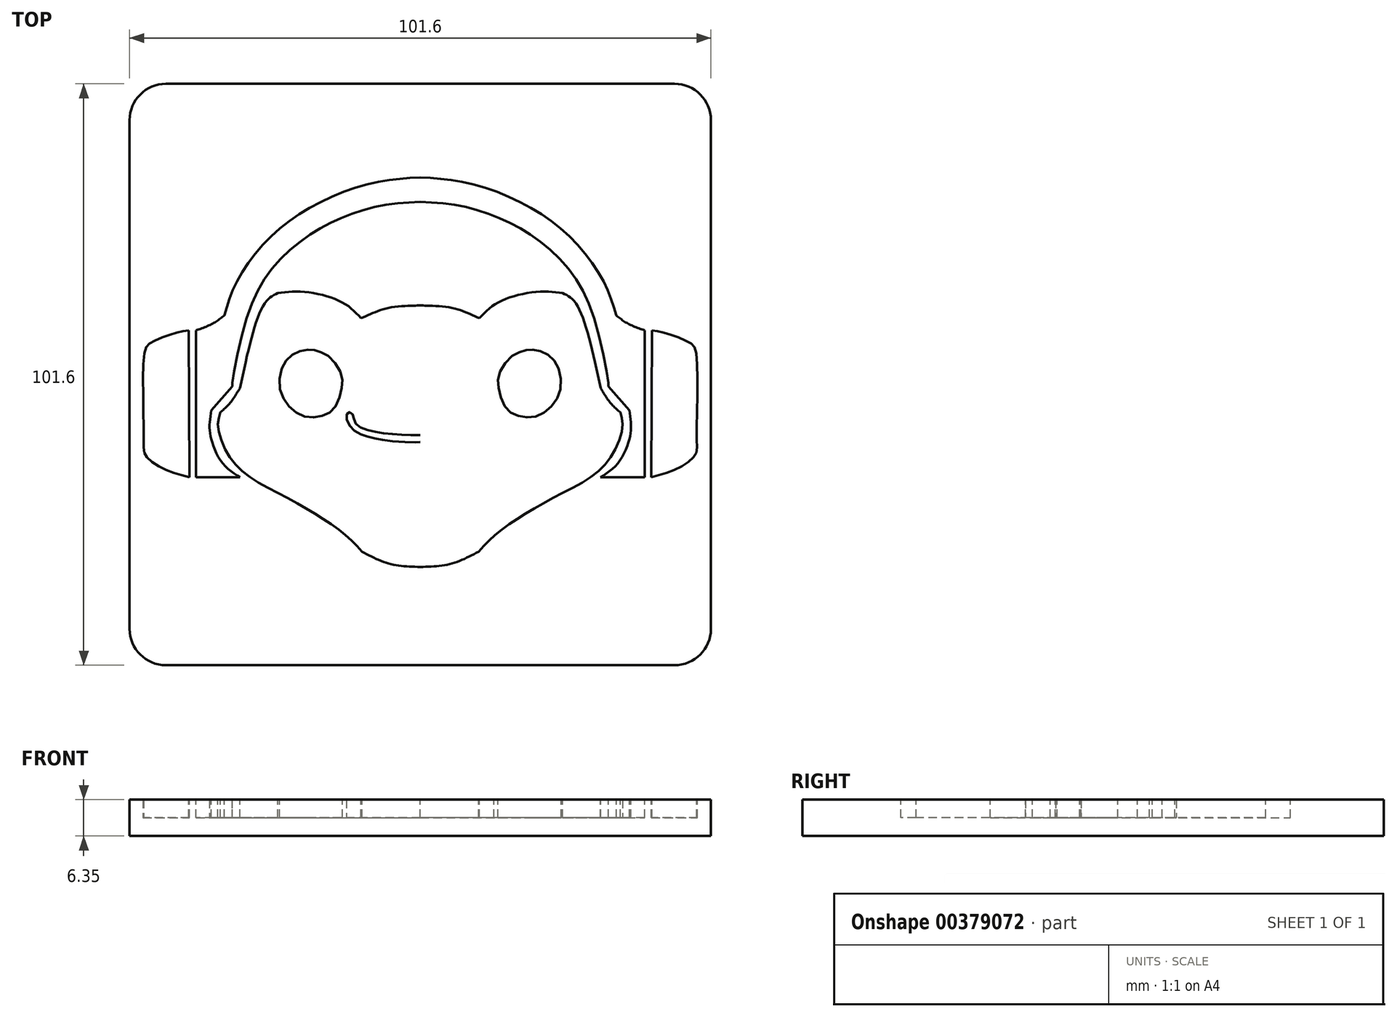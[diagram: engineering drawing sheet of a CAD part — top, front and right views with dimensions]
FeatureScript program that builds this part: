
annotation { "Feature Type Name" : "Feature", "Feature Type Description" : "" }
export const myFeature = defineFeature(function(context is Context, id is Id, definition is map)
    precondition{}
    {
        {
            var Q0;
            Q0=qCreatedBy(makeId("Top.planeOp"),FACE);
            var sketch = newSketch(context, id + "F0", { "sketchPlane" : qUnion([Q0])});
            skLineSegment(sketch, "E0.bottom", {"start": v(-44.45, 50.8) * mm, "end": v(44.45, 50.8) * mm});
            skLineSegment(sketch, "E0.top", {"start": v(-44.45, -50.8) * mm, "end": v(44.45, -50.8) * mm});
            skLineSegment(sketch, "E0.left", {"start": v(-50.8, 44.45) * mm, "end": v(-50.8, -44.45) * mm});
            skLineSegment(sketch, "E0.right", {"start": v(50.8, 44.45) * mm, "end": v(50.8, -44.45) * mm});
            skPoint(sketch, "E1.visualSharp", {"position": v(-50.8, 50.8) * mm});
            skArc(sketch, "E1.filletArc", {"start": v(-44.45, 50.8) * mm, "mid": v(-48.94, 48.94) * mm, "end": v(-50.8, 44.45) * mm});
            skPoint(sketch, "E2.visualSharp", {"position": v(50.8, 50.8) * mm});
            skArc(sketch, "E2.filletArc", {"start": v(50.8, 44.45) * mm, "mid": v(48.94, 48.94) * mm, "end": v(44.45, 50.8) * mm});
            skPoint(sketch, "E3.visualSharp", {"position": v(-50.8, -50.8) * mm});
            skArc(sketch, "E3.filletArc", {"start": v(-50.8, -44.45) * mm, "mid": v(-48.94, -48.94) * mm, "end": v(-44.45, -50.8) * mm});
            skPoint(sketch, "E4.visualSharp", {"position": v(50.8, -50.8) * mm});
            skArc(sketch, "E4.filletArc", {"start": v(44.45, -50.8) * mm, "mid": v(48.94, -48.94) * mm, "end": v(50.8, -44.45) * mm});
            skSolve(sketch);
        }
        {
            var Q0;
            Q0 = qSketchRegion(id + "F0", true);
            extrude(context, id + "F1", {"entities" : qUnion([Q0]), "depth" : 6.35 * mm});
        }
        {
            var Q0;
            Q0=makeQuery(id+"F1.opExtrude","CAP_FACE",FACE,{"disambiguationData":[OSD([sQuery(id+"F0.wireOp",EDGE,"E0.bottom"),sQuery(id+"F0.wireOp",EDGE,"E0.top"),sQuery(id+"F0.wireOp",EDGE,"E0.left"),sQuery(id+"F0.wireOp",EDGE,"E0.right"),sQuery(id+"F0.wireOp",EDGE,"E1.filletArc"),sQuery(id+"F0.wireOp",EDGE,"E2.filletArc"),sQuery(id+"F0.wireOp",EDGE,"E3.filletArc"),sQuery(id+"F0.wireOp",EDGE,"E4.filletArc")])],"isStart":false});
            var sketch = newSketch(context, id + "F2", { "sketchPlane" : qUnion([Q0])});
            skFitSpline(sketch, "E5", {"points": [v(-24.89, 14.25) * mm, v(-27.23, 12.37) * mm, v(-31.52, -2.38) * mm], "startDerivative": vector(-7.87, -3.8) * mm, "endDerivative": vector(-5.68, -26.52) * mm});
            skFitSpline(sketch, "E6", {"points": [v(-31.52, -2.38) * mm, v(-33.26, -5) * mm, v(-34.94, -6.6) * mm], "startDerivative": vector(-3.14, -5.23) * mm, "endDerivative": vector(-3.71, -3.16) * mm});
            skFitSpline(sketch, "E7", {"points": [v(-34.94, -6.6) * mm, v(-35.36, -9) * mm, v(-33.65, -13.85) * mm, v(-29.88, -17.88) * mm, v(-23.23, -21.57) * mm, v(-17.3, -25.03) * mm, v(-12.94, -28.16) * mm, v(-10.2, -30.95) * mm], "startDerivative": vector(-7.2, -21.92) * mm, "endDerivative": vector(20.36, -22.6) * mm});
            skFitSpline(sketch, "E8", {"points": [v(-10.2, -30.95) * mm, v(-5.4, -33.06) * mm, v(0, -33.63) * mm], "startDerivative": vector(9.4, -5.03) * mm, "endDerivative": vector(10.97, -0.34) * mm});
            skFitSpline(sketch, "E9", {"points": [v(-24.89, 14.25) * mm, v(-21.4, 14.5) * mm, v(-16.37, 13.7) * mm, v(-12.62, 11.97) * mm, v(-10.36, 9.83) * mm], "startDerivative": vector(13.95, 1.85) * mm, "endDerivative": vector(9.25, -10.17) * mm});
            skFitSpline(sketch, "E10", {"points": [v(-10.36, 9.83) * mm, v(-8, 10.86) * mm, v(-4.88, 11.76) * mm, v(-1.13, 12.04) * mm, v(0, 12.06) * mm], "startDerivative": vector(9.19, 4.21) * mm, "endDerivative": vector(5.68, 0.03) * mm});
            skFitSpline(sketch, "E11", {"points": [v(-19.65, 4.33) * mm, v(-22.07, 3.64) * mm, v(-23.97, 1.58) * mm, v(-24.54, -2.38) * mm, v(-22.9, -5.56) * mm, v(-20.13, -7.33) * mm, v(-17.2, -7.26) * mm, v(-14.99, -5.87) * mm, v(-13.75, -2.55) * mm, v(-13.78, 0) * mm, v(-15.84, 3.05) * mm, v(-18.04, 4.14) * mm, v(-19.65, 4.33) * mm]});
            skFitSpline(sketch, "E12", {"points": [v(0, -10.6) * mm, v(-5.07, -10.4) * mm, v(-9.16, -9.73) * mm, v(-11.3, -8.53) * mm, v(-11.74, -7.1) * mm, v(-12.43, -6.56) * mm, v(-12.9, -7.3) * mm, v(-11.85, -9.5) * mm, v(-9.16, -10.87) * mm, v(-5.1, -11.61) * mm, v(0, -11.8) * mm, v(0, -11.77) * mm], "startDerivative": vector(-38.3, 0.78) * mm, "endDerivative": vector(-1.42, 2.68) * mm});
            skFitSpline(sketch, "E13", {"points": [v(0, 30.15) * mm, v(-6.76, 29.52) * mm, v(-13.7, 27.37) * mm, v(-19.95, 23.97) * mm, v(-26.25, 18.03) * mm, v(-30.84, 8.17) * mm, v(-32.9, -2.1) * mm, v(-32.86, -2.1) * mm], "startDerivative": vector(-45.5, -2.07) * mm, "endDerivative": vector(3.29, 1.57) * mm});
            skFitSpline(sketch, "E14", {"points": [v(-32.86, -2.1) * mm, v(-36.53, -6.27) * mm], "startDerivative": vector(-3.67, -4.17) * mm, "endDerivative": vector(-3.67, -4.17) * mm});
            skFitSpline(sketch, "E15", {"points": [v(-36.53, -6.27) * mm, v(-36.82, -8.85) * mm, v(-36.53, -11.28) * mm, v(-34.68, -15.33) * mm, v(-31.5, -17.97) * mm], "startDerivative": vector(-1.76, -12.05) * mm, "endDerivative": vector(12.4, -8.07) * mm});
            skFitSpline(sketch, "E16", {"points": [v(-31.5, -17.97) * mm, v(-39.2, -17.97) * mm], "startDerivative": vector(-7.7, 0) * mm, "endDerivative": vector(-7.7, 0) * mm});
            skFitSpline(sketch, "E17", {"points": [v(-39.2, -17.97) * mm, v(-39.2, 7.71) * mm], "startDerivative": vector(0, 25.68) * mm, "endDerivative": vector(0, 25.68) * mm});
            skFitSpline(sketch, "E18", {"points": [v(-39.2, 7.71) * mm, v(-36.25, 8.92) * mm, v(-34.25, 10.33) * mm], "startDerivative": vector(5.86, 2.07) * mm, "endDerivative": vector(4, 3.2) * mm});
            skFitSpline(sketch, "E19", {"points": [v(-34.25, 10.33) * mm, v(-32.22, 15.9) * mm, v(-26.86, 23.35) * mm, v(-18.57, 29.56) * mm, v(-8.1, 33.54) * mm, v(0, 34.44) * mm], "startDerivative": vector(9.67, 33.1) * mm, "endDerivative": vector(40.71, 2.06) * mm});
            skFitSpline(sketch, "E20", {"points": [v(-40.47, 7.71) * mm, v(-40.36, -17.97) * mm], "startDerivative": vector(0.11, -25.68) * mm, "endDerivative": vector(0.11, -25.68) * mm});
            skFitSpline(sketch, "E21", {"points": [v(-40.36, -17.97) * mm, v(-44.84, -16.46) * mm, v(-48.01, -14.14) * mm, v(-48.33, -11.36) * mm, v(-48.25, 3.65) * mm, v(-47.12, 5.54) * mm, v(-43.26, 7.12) * mm, v(-40.47, 7.71) * mm], "startDerivative": vector(-30.96, 8.3) * mm, "endDerivative": vector(22.64, 3.58) * mm});
            skFitSpline(sketch, "E22.MirrorCS", {"points": [v(34.25, 10.33) * mm, v(32.22, 15.9) * mm, v(26.86, 23.35) * mm, v(18.57, 29.56) * mm, v(8.1, 33.54) * mm, v(0, 34.44) * mm], "startDerivative": vector(-9.67, 33.1) * mm, "endDerivative": vector(-40.71, 2.06) * mm});
            skFitSpline(sketch, "E23.MirrorCS", {"points": [v(0, 30.15) * mm, v(6.76, 29.52) * mm, v(13.7, 27.37) * mm, v(19.95, 23.97) * mm, v(26.25, 18.03) * mm, v(30.84, 8.17) * mm, v(32.9, -2.1) * mm, v(32.86, -2.1) * mm], "startDerivative": vector(45.5, -2.07) * mm, "endDerivative": vector(-3.29, 1.57) * mm});
            skFitSpline(sketch, "E24.MirrorCS", {"points": [v(10.36, 9.83) * mm, v(8, 10.86) * mm, v(4.88, 11.76) * mm, v(1.13, 12.04) * mm, v(0, 12.06) * mm], "startDerivative": vector(-9.19, 4.21) * mm, "endDerivative": vector(-5.68, 0.03) * mm});
            skFitSpline(sketch, "E25.MirrorCS", {"points": [v(24.89, 14.25) * mm, v(21.4, 14.5) * mm, v(16.37, 13.7) * mm, v(12.62, 11.97) * mm, v(10.36, 9.83) * mm], "startDerivative": vector(-13.95, 1.85) * mm, "endDerivative": vector(-9.25, -10.17) * mm});
            skFitSpline(sketch, "E26.MirrorCS", {"points": [v(24.89, 14.25) * mm, v(27.23, 12.37) * mm, v(31.52, -2.38) * mm], "startDerivative": vector(7.87, -3.8) * mm, "endDerivative": vector(5.68, -26.52) * mm});
            skFitSpline(sketch, "E27.MirrorCS", {"points": [v(31.52, -2.38) * mm, v(33.26, -5) * mm, v(34.94, -6.6) * mm], "startDerivative": vector(3.14, -5.23) * mm, "endDerivative": vector(3.71, -3.16) * mm});
            skFitSpline(sketch, "E28.MirrorCS", {"points": [v(34.94, -6.6) * mm, v(35.36, -9) * mm, v(33.65, -13.85) * mm, v(29.88, -17.88) * mm, v(23.23, -21.57) * mm, v(17.3, -25.03) * mm, v(12.94, -28.16) * mm, v(10.2, -30.95) * mm], "startDerivative": vector(7.2, -21.92) * mm, "endDerivative": vector(-20.36, -22.6) * mm});
            skFitSpline(sketch, "E29.MirrorCS", {"points": [v(10.2, -30.95) * mm, v(5.4, -33.06) * mm, v(0, -33.63) * mm], "startDerivative": vector(-9.4, -5.03) * mm, "endDerivative": vector(-10.97, -0.34) * mm});
            skFitSpline(sketch, "E30.MirrorCS", {"points": [v(0, -10.6) * mm, v(5.07, -10.4) * mm, v(9.16, -9.73) * mm, v(11.3, -8.53) * mm, v(11.74, -7.1) * mm, v(12.43, -6.56) * mm, v(12.9, -7.3) * mm, v(11.85, -9.5) * mm, v(9.16, -10.87) * mm, v(5.1, -11.61) * mm, v(0, -11.8) * mm, v(0, -11.77) * mm], "startDerivative": vector(38.3, 0.78) * mm, "endDerivative": vector(1.42, 2.68) * mm});
            skFitSpline(sketch, "E31.MirrorC", {"points": [v(19.65, 4.33) * mm, v(22.07, 3.64) * mm, v(23.97, 1.58) * mm, v(24.54, -2.38) * mm, v(22.9, -5.56) * mm, v(20.13, -7.33) * mm, v(17.2, -7.26) * mm, v(14.99, -5.87) * mm, v(13.75, -2.55) * mm, v(13.78, 0) * mm, v(15.84, 3.05) * mm, v(18.04, 4.14) * mm, v(19.65, 4.33) * mm]});
            skFitSpline(sketch, "E32.MirrorCS", {"points": [v(39.2, -17.97) * mm, v(39.2, 7.71) * mm], "startDerivative": vector(0, 25.68) * mm, "endDerivative": vector(0, 25.68) * mm});
            skFitSpline(sketch, "E33.MirrorCS", {"points": [v(39.2, 7.71) * mm, v(36.25, 8.92) * mm, v(34.25, 10.33) * mm], "startDerivative": vector(-5.86, 2.07) * mm, "endDerivative": vector(-4, 3.2) * mm});
            skFitSpline(sketch, "E34.MirrorCS", {"points": [v(32.86, -2.1) * mm, v(36.53, -6.27) * mm], "startDerivative": vector(3.67, -4.17) * mm, "endDerivative": vector(3.67, -4.17) * mm});
            skFitSpline(sketch, "E35.MirrorCS", {"points": [v(36.53, -6.27) * mm, v(36.82, -8.85) * mm, v(36.53, -11.28) * mm, v(34.68, -15.33) * mm, v(31.5, -17.97) * mm], "startDerivative": vector(1.76, -12.05) * mm, "endDerivative": vector(-12.4, -8.07) * mm});
            skFitSpline(sketch, "E36.MirrorCS", {"points": [v(31.5, -17.97) * mm, v(39.2, -17.97) * mm], "startDerivative": vector(7.7, 0) * mm, "endDerivative": vector(7.7, 0) * mm});
            skFitSpline(sketch, "E37.MirrorCS", {"points": [v(40.47, 7.71) * mm, v(40.36, -17.97) * mm], "startDerivative": vector(-0.11, -25.68) * mm, "endDerivative": vector(-0.11, -25.68) * mm});
            skFitSpline(sketch, "E38.MirrorCS", {"points": [v(40.36, -17.97) * mm, v(44.84, -16.46) * mm, v(48.01, -14.14) * mm, v(48.33, -11.36) * mm, v(48.25, 3.65) * mm, v(47.12, 5.54) * mm, v(43.26, 7.12) * mm, v(40.47, 7.71) * mm], "startDerivative": vector(30.96, 8.3) * mm, "endDerivative": vector(-22.64, 3.58) * mm});
            skSolve(sketch);
        }
        {
            var Q0;
            Q0 = qSketchRegion(id + "F2", true);
            extrude(context, id + "F3", {"entities" : qUnion([Q0]), "operationType" : NewBodyOperationType.REMOVE, "oppositeDirection" : true, "depth" : 3.17 * mm});
        }
    });
